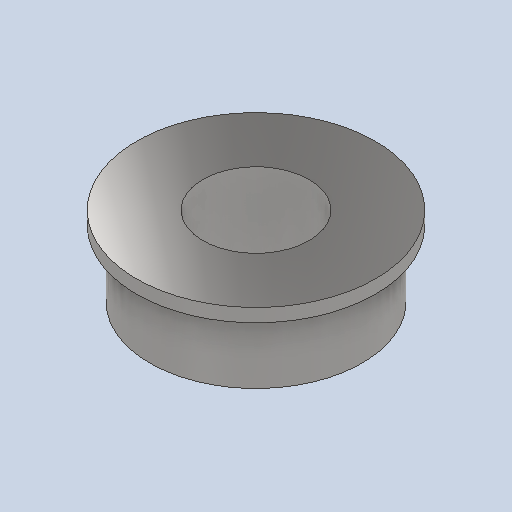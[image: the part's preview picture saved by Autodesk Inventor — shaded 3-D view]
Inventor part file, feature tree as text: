
AUTODESK INVENTOR PART (.ipt)
format: ipt  version: 2022 (Build 260153000, 153)  size: 143,360 bytes
history: native  units: mm
features: extrude x3, sketch x3, other x1
ambient origin geometry x8: Origin, YZ Plane, XZ Plane, XY Plane, X Axis, Y Axis, Z Axis, Center Point
bodies: Body1 (feature_tree)
feature tree (7):
  other  "ソリッド1"
  extrude  "押し出し1"  Depth=8.0mm
  extrude  "押し出し2"  Depth=2.5mm TaperAngle=0.0deg
  extrude  "押し出し3"  Depth=9.0mm
  sketch  "スケッチ1"
  sketch  "スケッチ2"
  sketch  "スケッチ3"
